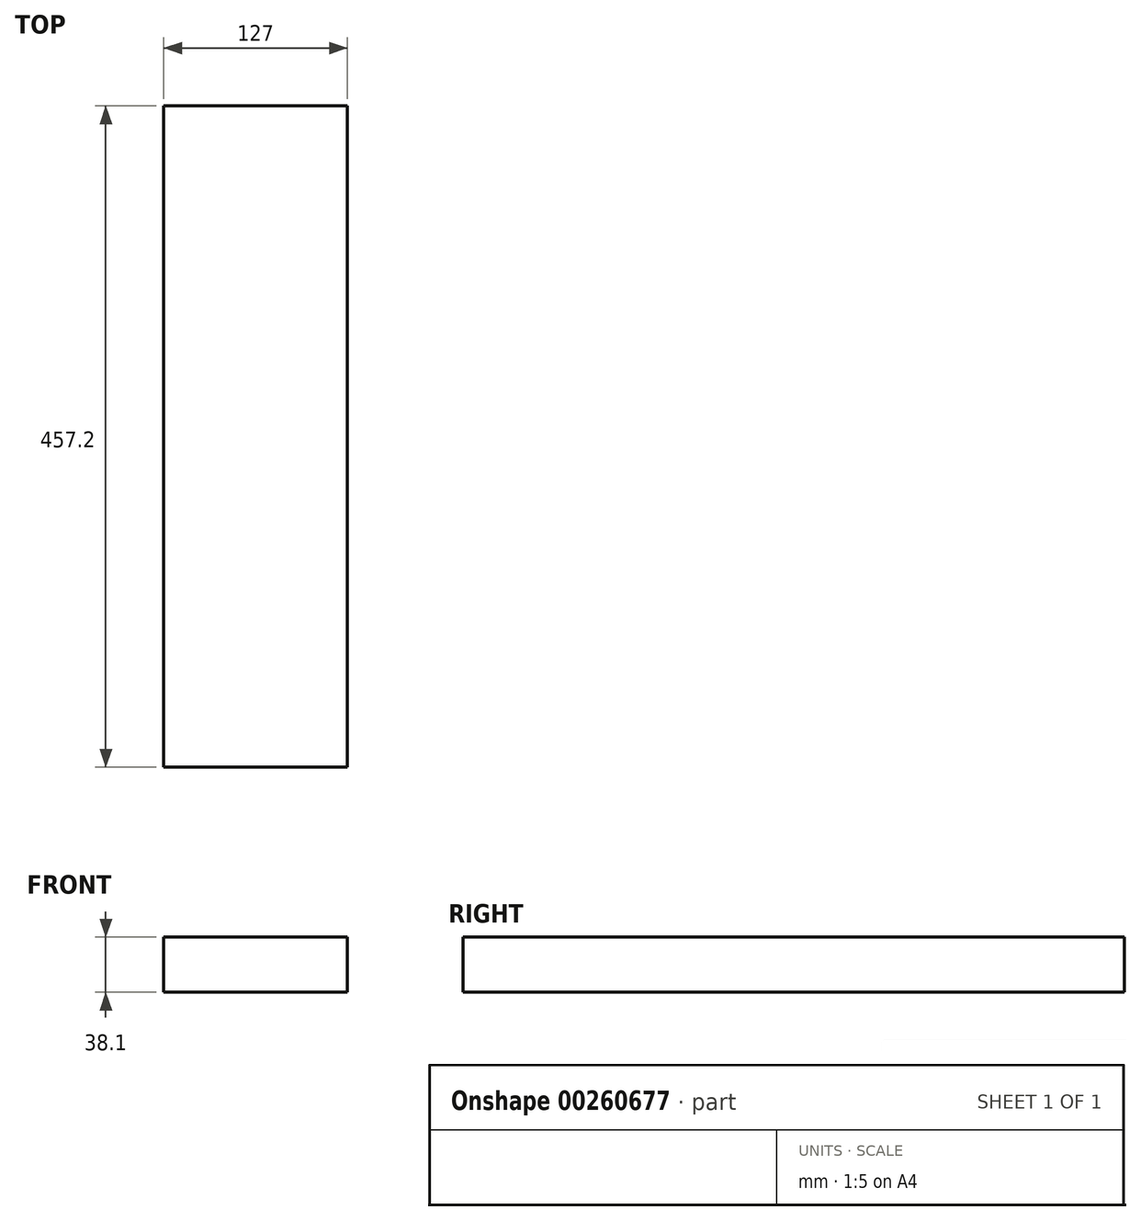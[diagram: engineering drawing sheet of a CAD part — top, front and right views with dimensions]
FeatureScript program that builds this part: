
annotation { "Feature Type Name" : "Feature", "Feature Type Description" : "" }
export const myFeature = defineFeature(function(context is Context, id is Id, definition is map)
    precondition{}
    {
        {
            var Q0;
            Q0=qCreatedBy(makeId("Front.planeOp"),FACE);
            var sketch = newSketch(context, id + "F0", { "sketchPlane" : qUnion([Q0])});
            skLineSegment(sketch, "E0", {"start": v(-34.46, 34.3) * mm, "end": v(-34.46, -3.8) * mm});
            skLineSegment(sketch, "E1", {"start": v(-34.46, -3.8) * mm, "end": v(92.54, -3.8) * mm});
            skLineSegment(sketch, "E2", {"start": v(92.54, -3.8) * mm, "end": v(92.54, 34.3) * mm});
            skLineSegment(sketch, "E3", {"start": v(92.54, 34.3) * mm, "end": v(-34.46, 34.3) * mm});
            skSolve(sketch);
        }
        {
            var Q0;
            Q0=makeQuery(id+"F0.imprint","IMPRINT",FACE,{"disambiguationData":[TD([[makeQuery(id+"F0.imprint","IMPRINT",EDGE,{"derivedFrom":sQuery(id+"F0.wireOp",EDGE,"E0")}),1.0]])]});
            extrude(context, id + "F1", {"entities" : qUnion([Q0]), "depth" : 457.2 * mm});
        }
    });
